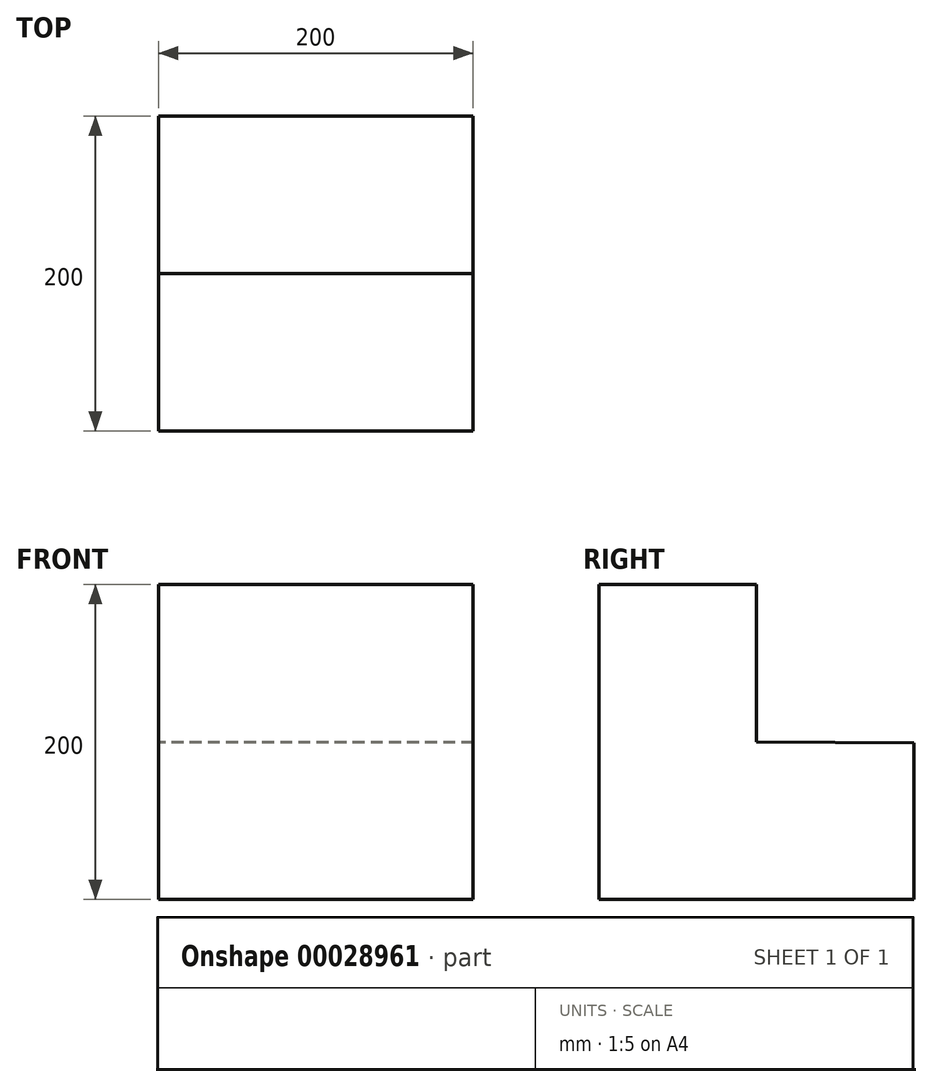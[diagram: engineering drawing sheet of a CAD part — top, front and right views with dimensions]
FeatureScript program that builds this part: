
annotation { "Feature Type Name" : "Feature", "Feature Type Description" : "" }
export const myFeature = defineFeature(function(context is Context, id is Id, definition is map)
    precondition{}
    {
        {
            var Q0;
            Q0=qCreatedBy(makeId("Right.planeOp"),FACE);
            var sketch = newSketch(context, id + "F0", { "sketchPlane" : qUnion([Q0])});
            skLineSegment(sketch, "E0", {"start": v(0, 0) * mm, "end": v(0, 200) * mm});
            skLineSegment(sketch, "E1", {"start": v(0, 200) * mm, "end": v(100, 200) * mm});
            skLineSegment(sketch, "E2", {"start": v(100, 200) * mm, "end": v(100, 100) * mm});
            skLineSegment(sketch, "E3", {"start": v(100, 100) * mm, "end": v(200, 99.25) * mm});
            skLineSegment(sketch, "E4", {"start": v(200, 99.25) * mm, "end": v(200, 0) * mm});
            skLineSegment(sketch, "E5", {"start": v(200, 0) * mm, "end": v(0, 0) * mm});
            skSolve(sketch);
        }
        {
            var Q0;
            Q0=makeQuery(id+"F0.imprint","IMPRINT",FACE,{"disambiguationData":[TD([[makeQuery(id+"F0.imprint","IMPRINT",EDGE,{"derivedFrom":sQuery(id+"F0.wireOp",EDGE,"E0")}),-1.0]])]});
            extrude(context, id + "F1", {"entities" : qUnion([Q0]), "depth" : 200 * mm});
        }
    });
